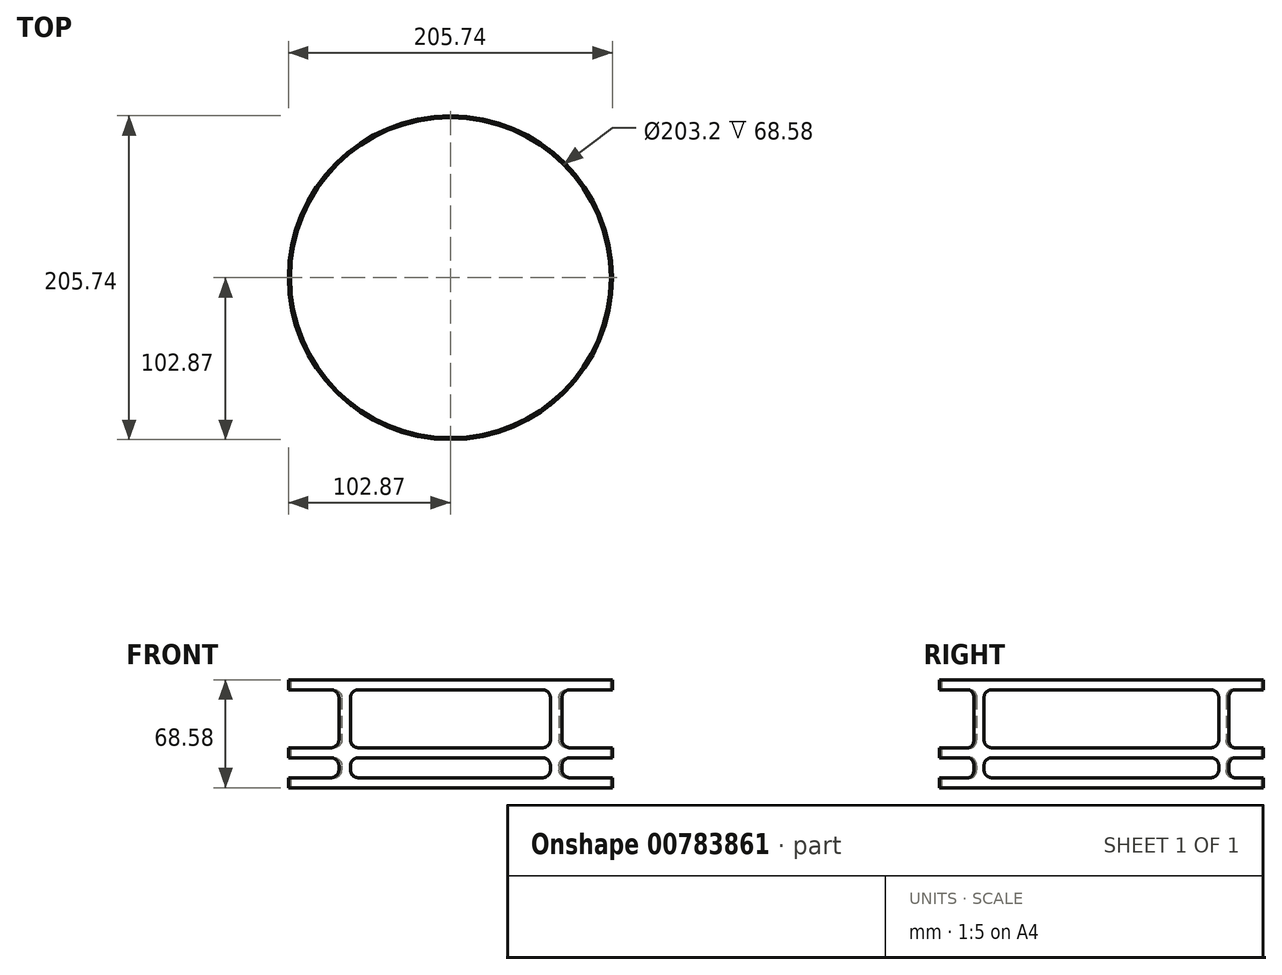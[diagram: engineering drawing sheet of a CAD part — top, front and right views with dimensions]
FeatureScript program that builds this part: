
annotation { "Feature Type Name" : "Feature", "Feature Type Description" : "" }
export const myFeature = defineFeature(function(context is Context, id is Id, definition is map)
    precondition{}
    {
        {
            var Q0;
            Q0=qCreatedBy(makeId("Top.planeOp"),FACE);
            var sketch = newSketch(context, id + "F0", { "sketchPlane" : qUnion([Q0])});
            skCircle(sketch, "E0", {"center": v(0, 0) * mm, "radius": 101.6 * mm});
            skCircle(sketch, "E1", {"center": v(0, 0) * mm, "radius": 102.87 * mm});
            skSolve(sketch);
        }
        {
            var Q0;
            Q0 = qSketchRegion(id + "F0", true);
            extrude(context, id + "F1", {"entities" : qUnion([Q0]), "depth" : 68.58 * mm, "offsetDistance" : 25.4 * mm});
        }
        {
            var Q0;
            Q0=qCreatedBy(makeId("Front.planeOp"),FACE);
            var sketch = newSketch(context, id + "F2", { "sketchPlane" : qUnion([Q0])});
            skLineSegment(sketch, "E2", {"start": v(-102.87, 0) * mm, "end": v(-102.87, 68.58) * mm, "construction": true});
            skLineSegment(sketch, "E3", {"start": v(102.87, 68.58) * mm, "end": v(102.87, 0) * mm, "construction": true});
            skLineSegment(sketch, "E4.0", {"start": v(-102.87, 0) * mm, "end": v(102.87, 0) * mm, "construction": true});
            skLineSegment(sketch, "E5", {"start": v(0, 0) * mm, "end": v(0, 25.4) * mm, "construction": true});
            skLineSegment(sketch, "E6.bottom", {"start": v(63.5, 6.35) * mm, "end": v(-63.5, 6.35) * mm});
            skLineSegment(sketch, "E6.top", {"start": v(63.5, 19.05) * mm, "end": v(-63.5, 19.05) * mm});
            skLineSegment(sketch, "E6.left", {"start": v(63.5, 6.35) * mm, "end": v(63.5, 19.05) * mm});
            skLineSegment(sketch, "E6.right", {"start": v(-63.5, 6.35) * mm, "end": v(-63.5, 19.05) * mm});
            skPoint(sketch, "E6.middle", {"position": v(0, 12.7) * mm});
            skLineSegment(sketch, "E7.0", {"start": v(-102.87, 68.58) * mm, "end": v(102.87, 68.58) * mm, "construction": true});
            skLineSegment(sketch, "E8", {"start": v(-63.5, 25.4) * mm, "end": v(-63.5, 62.23) * mm});
            skLineSegment(sketch, "E9", {"start": v(-63.5, 62.23) * mm, "end": v(63.5, 62.23) * mm});
            skLineSegment(sketch, "E10", {"start": v(63.5, 62.23) * mm, "end": v(63.5, 25.4) * mm});
            skLineSegment(sketch, "E11", {"start": v(63.5, 25.4) * mm, "end": v(-63.5, 25.4) * mm});
            skPoint(sketch, "E12.orphan", {"position": v(-63.5, 27.25) * mm});
            skSolve(sketch);
        }
        {
            var Q0;
            Q0 = qSketchRegion(id + "F2", true);
            extrude(context, id + "F3", {"entities" : qUnion([Q0]), "operationType" : NewBodyOperationType.REMOVE, "endBound" : BoundingType.THROUGH_ALL, "oppositeDirection" : true, "depth" : 25.4 * mm, "offsetDistance" : 25.4 * mm, "hasSecondDirection" : true, "secondDirectionBound" : BoundingType.THROUGH_ALL, "secondDirectionOppositeDirection" : false, "secondDirectionDepth" : 25.4 * mm});
        }
        {
            var Q0;
            Q0=qCreatedBy(makeId("Right.planeOp"),FACE);
            var sketch = newSketch(context, id + "F4", { "sketchPlane" : qUnion([Q0])});
            skLineSegment(sketch, "E13", {"start": v(-102.87, 0) * mm, "end": v(-102.87, 68.58) * mm, "construction": true});
            skLineSegment(sketch, "E14", {"start": v(102.87, 68.58) * mm, "end": v(102.87, 0) * mm, "construction": true});
            skLineSegment(sketch, "E15", {"start": v(0, 0) * mm, "end": v(0, 25.4) * mm, "construction": true});
            skLineSegment(sketch, "E16.bottom", {"start": v(74.58, 6.35) * mm, "end": v(-74.58, 6.35) * mm});
            skLineSegment(sketch, "E16.top", {"start": v(74.58, 19.05) * mm, "end": v(-74.58, 19.05) * mm});
            skLineSegment(sketch, "E16.left", {"start": v(74.58, 6.35) * mm, "end": v(74.58, 19.05) * mm});
            skLineSegment(sketch, "E16.right", {"start": v(-74.58, 6.35) * mm, "end": v(-74.58, 19.05) * mm});
            skPoint(sketch, "E16.middle", {"position": v(0, 12.7) * mm});
            skLineSegment(sketch, "E17.0", {"start": v(-102.87, 68.58) * mm, "end": v(102.87, 68.58) * mm, "construction": true});
            skLineSegment(sketch, "E18.0", {"start": v(-80.93, 25.4) * mm, "end": v(-80.93, 62.23) * mm, "construction": true});
            skLineSegment(sketch, "E19.0", {"start": v(80.93, 62.23) * mm, "end": v(80.93, 25.4) * mm, "construction": true});
            skLineSegment(sketch, "E20.bottom", {"start": v(-74.58, 25.4) * mm, "end": v(74.58, 25.4) * mm});
            skLineSegment(sketch, "E20.top", {"start": v(-74.58, 62.23) * mm, "end": v(74.58, 62.23) * mm});
            skLineSegment(sketch, "E20.left", {"start": v(-74.58, 25.4) * mm, "end": v(-74.58, 62.23) * mm});
            skLineSegment(sketch, "E20.right", {"start": v(74.58, 25.4) * mm, "end": v(74.58, 62.23) * mm});
            skSolve(sketch);
        }
        {
            var Q0;
            Q0 = qSketchRegion(id + "F4", true);
            extrude(context, id + "F5", {"entities" : qUnion([Q0]), "operationType" : NewBodyOperationType.REMOVE, "endBound" : BoundingType.THROUGH_ALL, "oppositeDirection" : true, "depth" : 25.4 * mm, "offsetDistance" : 25.4 * mm, "hasSecondDirection" : true, "secondDirectionBound" : BoundingType.THROUGH_ALL, "secondDirectionOppositeDirection" : false, "secondDirectionDepth" : 25.4 * mm});
        }
        {
            var Q0;
            Q0=makeQuery(id+"F3.boolean.opBoolean","COPY",EDGE,{"disambiguationData":[OD(0.0)],"derivedFrom":makeQuery(id+"F3.opExtrude","SWEPT_EDGE",EDGE,{"disambiguationData":[OSD([sQuery(id+"F2.wireOp",EDGE,"E6.top"),sQuery(id+"F2.wireOp",EDGE,"E6.right")])]})});
            var Q1;
            Q1=makeQuery(id+"F3.boolean.opBoolean","COPY",EDGE,{"disambiguationData":[OD(0.0)],"derivedFrom":makeQuery(id+"F3.opExtrude","SWEPT_EDGE",EDGE,{"disambiguationData":[OSD([sQuery(id+"F2.wireOp",EDGE,"E6.bottom"),sQuery(id+"F2.wireOp",EDGE,"E6.right")])]})});
            var Q2;
            Q2=makeQuery(id+"F3.boolean.opBoolean","COPY",EDGE,{"disambiguationData":[OD(0.0)],"derivedFrom":makeQuery(id+"F3.opExtrude","SWEPT_EDGE",EDGE,{"disambiguationData":[OSD([sQuery(id+"F2.wireOp",EDGE,"E6.top"),sQuery(id+"F2.wireOp",EDGE,"E6.left")])]})});
            var Q3;
            Q3=makeQuery(id+"F3.boolean.opBoolean","COPY",EDGE,{"disambiguationData":[OD(0.0)],"derivedFrom":makeQuery(id+"F3.opExtrude","SWEPT_EDGE",EDGE,{"disambiguationData":[OSD([sQuery(id+"F2.wireOp",EDGE,"E6.bottom"),sQuery(id+"F2.wireOp",EDGE,"E6.left")])]})});
            var Q4;
            Q4=makeQuery(id+"F5.boolean.opBoolean","COPY",EDGE,{"disambiguationData":[OD(1.0)],"derivedFrom":makeQuery(id+"F5.opExtrude","SWEPT_EDGE",EDGE,{"disambiguationData":[OSD([sQuery(id+"F4.wireOp",EDGE,"E16.top"),sQuery(id+"F4.wireOp",EDGE,"E16.right")])]})});
            var Q5;
            Q5=makeQuery(id+"F5.boolean.opBoolean","COPY",EDGE,{"disambiguationData":[OD(1.0)],"derivedFrom":makeQuery(id+"F5.opExtrude","SWEPT_EDGE",EDGE,{"disambiguationData":[OSD([sQuery(id+"F4.wireOp",EDGE,"E16.bottom"),sQuery(id+"F4.wireOp",EDGE,"E16.right")])]})});
            var Q6;
            Q6=makeQuery(id+"F5.boolean.opBoolean","COPY",EDGE,{"disambiguationData":[OD(1.0)],"derivedFrom":makeQuery(id+"F5.opExtrude","SWEPT_EDGE",EDGE,{"disambiguationData":[OSD([sQuery(id+"F4.wireOp",EDGE,"E16.top"),sQuery(id+"F4.wireOp",EDGE,"E16.left")])]})});
            var Q7;
            Q7=makeQuery(id+"F5.boolean.opBoolean","COPY",EDGE,{"disambiguationData":[OD(1.0)],"derivedFrom":makeQuery(id+"F5.opExtrude","SWEPT_EDGE",EDGE,{"disambiguationData":[OSD([sQuery(id+"F4.wireOp",EDGE,"E16.bottom"),sQuery(id+"F4.wireOp",EDGE,"E16.left")])]})});
            var Q8;
            Q8=makeQuery(id+"F3.boolean.opBoolean","COPY",EDGE,{"disambiguationData":[OD(1.0)],"derivedFrom":makeQuery(id+"F3.opExtrude","SWEPT_EDGE",EDGE,{"disambiguationData":[OSD([sQuery(id+"F2.wireOp",EDGE,"E6.bottom"),sQuery(id+"F2.wireOp",EDGE,"E6.left")])]})});
            var Q9;
            Q9=makeQuery(id+"F3.boolean.opBoolean","COPY",EDGE,{"disambiguationData":[OD(1.0)],"derivedFrom":makeQuery(id+"F3.opExtrude","SWEPT_EDGE",EDGE,{"disambiguationData":[OSD([sQuery(id+"F2.wireOp",EDGE,"E6.top"),sQuery(id+"F2.wireOp",EDGE,"E6.left")])]})});
            var Q10;
            Q10=makeQuery(id+"F3.boolean.opBoolean","COPY",EDGE,{"disambiguationData":[OD(1.0)],"derivedFrom":makeQuery(id+"F3.opExtrude","SWEPT_EDGE",EDGE,{"disambiguationData":[OSD([sQuery(id+"F2.wireOp",EDGE,"E6.bottom"),sQuery(id+"F2.wireOp",EDGE,"E6.right")])]})});
            var Q11;
            Q11=makeQuery(id+"F3.boolean.opBoolean","COPY",EDGE,{"disambiguationData":[OD(1.0)],"derivedFrom":makeQuery(id+"F3.opExtrude","SWEPT_EDGE",EDGE,{"disambiguationData":[OSD([sQuery(id+"F2.wireOp",EDGE,"E6.top"),sQuery(id+"F2.wireOp",EDGE,"E6.right")])]})});
            var Q12;
            Q12=makeQuery(id+"F5.boolean.opBoolean","COPY",EDGE,{"disambiguationData":[OD(0.0)],"derivedFrom":makeQuery(id+"F5.opExtrude","SWEPT_EDGE",EDGE,{"disambiguationData":[OSD([sQuery(id+"F4.wireOp",EDGE,"E16.bottom"),sQuery(id+"F4.wireOp",EDGE,"E16.left")])]})});
            var Q13;
            Q13=makeQuery(id+"F5.boolean.opBoolean","COPY",EDGE,{"disambiguationData":[OD(0.0)],"derivedFrom":makeQuery(id+"F5.opExtrude","SWEPT_EDGE",EDGE,{"disambiguationData":[OSD([sQuery(id+"F4.wireOp",EDGE,"E16.top"),sQuery(id+"F4.wireOp",EDGE,"E16.left")])]})});
            var Q14;
            Q14=makeQuery(id+"F5.boolean.opBoolean","COPY",EDGE,{"disambiguationData":[OD(0.0)],"derivedFrom":makeQuery(id+"F5.opExtrude","SWEPT_EDGE",EDGE,{"disambiguationData":[OSD([sQuery(id+"F4.wireOp",EDGE,"E16.bottom"),sQuery(id+"F4.wireOp",EDGE,"E16.right")])]})});
            var Q15;
            Q15=makeQuery(id+"F5.boolean.opBoolean","COPY",EDGE,{"disambiguationData":[OD(0.0)],"derivedFrom":makeQuery(id+"F5.opExtrude","SWEPT_EDGE",EDGE,{"disambiguationData":[OSD([sQuery(id+"F4.wireOp",EDGE,"E16.top"),sQuery(id+"F4.wireOp",EDGE,"E16.right")])]})});
            var Q16;
            Q16=makeQuery(id+"F3.boolean.opBoolean","COPY",EDGE,{"disambiguationData":[OD(0.0)],"derivedFrom":makeQuery(id+"F3.opExtrude","SWEPT_EDGE",EDGE,{"disambiguationData":[OSD([sQuery(id+"F2.wireOp",EDGE,"E8"),sQuery(id+"F2.wireOp",EDGE,"E11")])]})});
            var Q17;
            Q17=makeQuery(id+"F3.boolean.opBoolean","COPY",EDGE,{"disambiguationData":[OD(0.0)],"derivedFrom":makeQuery(id+"F3.opExtrude","SWEPT_EDGE",EDGE,{"disambiguationData":[OSD([sQuery(id+"F2.wireOp",EDGE,"E8"),sQuery(id+"F2.wireOp",EDGE,"E9")])]})});
            var Q18;
            Q18=makeQuery(id+"F3.boolean.opBoolean","COPY",EDGE,{"disambiguationData":[OD(0.0)],"derivedFrom":makeQuery(id+"F3.opExtrude","SWEPT_EDGE",EDGE,{"disambiguationData":[OSD([sQuery(id+"F2.wireOp",EDGE,"E10"),sQuery(id+"F2.wireOp",EDGE,"E11")])]})});
            var Q19;
            Q19=makeQuery(id+"F3.boolean.opBoolean","COPY",EDGE,{"disambiguationData":[OD(0.0)],"derivedFrom":makeQuery(id+"F3.opExtrude","SWEPT_EDGE",EDGE,{"disambiguationData":[OSD([sQuery(id+"F2.wireOp",EDGE,"E9"),sQuery(id+"F2.wireOp",EDGE,"E10")])]})});
            var Q20;
            Q20=makeQuery(id+"F5.boolean.opBoolean","COPY",EDGE,{"disambiguationData":[OD(0.0)],"derivedFrom":makeQuery(id+"F5.opExtrude","SWEPT_EDGE",EDGE,{"disambiguationData":[OSD([sQuery(id+"F4.wireOp",EDGE,"E20.top"),sQuery(id+"F4.wireOp",EDGE,"E20.left")])]})});
            var Q21;
            Q21=makeQuery(id+"F5.boolean.opBoolean","COPY",EDGE,{"disambiguationData":[OD(0.0)],"derivedFrom":makeQuery(id+"F5.opExtrude","SWEPT_EDGE",EDGE,{"disambiguationData":[OSD([sQuery(id+"F4.wireOp",EDGE,"E20.bottom"),sQuery(id+"F4.wireOp",EDGE,"E20.left")])]})});
            var Q22;
            Q22=makeQuery(id+"F5.boolean.opBoolean","COPY",EDGE,{"disambiguationData":[OD(0.0)],"derivedFrom":makeQuery(id+"F5.opExtrude","SWEPT_EDGE",EDGE,{"disambiguationData":[OSD([sQuery(id+"F4.wireOp",EDGE,"E20.top"),sQuery(id+"F4.wireOp",EDGE,"E20.right")])]})});
            var Q23;
            Q23=makeQuery(id+"F5.boolean.opBoolean","COPY",EDGE,{"disambiguationData":[OD(0.0)],"derivedFrom":makeQuery(id+"F5.opExtrude","SWEPT_EDGE",EDGE,{"disambiguationData":[OSD([sQuery(id+"F4.wireOp",EDGE,"E20.bottom"),sQuery(id+"F4.wireOp",EDGE,"E20.right")])]})});
            var Q24;
            Q24=makeQuery(id+"F3.boolean.opBoolean","COPY",EDGE,{"disambiguationData":[OD(1.0)],"derivedFrom":makeQuery(id+"F3.opExtrude","SWEPT_EDGE",EDGE,{"disambiguationData":[OSD([sQuery(id+"F2.wireOp",EDGE,"E8"),sQuery(id+"F2.wireOp",EDGE,"E9")])]})});
            var Q25;
            Q25=makeQuery(id+"F3.boolean.opBoolean","COPY",EDGE,{"disambiguationData":[OD(1.0)],"derivedFrom":makeQuery(id+"F3.opExtrude","SWEPT_EDGE",EDGE,{"disambiguationData":[OSD([sQuery(id+"F2.wireOp",EDGE,"E8"),sQuery(id+"F2.wireOp",EDGE,"E11")])]})});
            var Q26;
            Q26=makeQuery(id+"F3.boolean.opBoolean","COPY",EDGE,{"disambiguationData":[OD(1.0)],"derivedFrom":makeQuery(id+"F3.opExtrude","SWEPT_EDGE",EDGE,{"disambiguationData":[OSD([sQuery(id+"F2.wireOp",EDGE,"E9"),sQuery(id+"F2.wireOp",EDGE,"E10")])]})});
            var Q27;
            Q27=makeQuery(id+"F3.boolean.opBoolean","COPY",EDGE,{"disambiguationData":[OD(1.0)],"derivedFrom":makeQuery(id+"F3.opExtrude","SWEPT_EDGE",EDGE,{"disambiguationData":[OSD([sQuery(id+"F2.wireOp",EDGE,"E10"),sQuery(id+"F2.wireOp",EDGE,"E11")])]})});
            var Q28;
            Q28=makeQuery(id+"F5.boolean.opBoolean","COPY",EDGE,{"disambiguationData":[OD(1.0)],"derivedFrom":makeQuery(id+"F5.opExtrude","SWEPT_EDGE",EDGE,{"disambiguationData":[OSD([sQuery(id+"F4.wireOp",EDGE,"E20.bottom"),sQuery(id+"F4.wireOp",EDGE,"E20.right")])]})});
            var Q29;
            Q29=makeQuery(id+"F5.boolean.opBoolean","COPY",EDGE,{"disambiguationData":[OD(1.0)],"derivedFrom":makeQuery(id+"F5.opExtrude","SWEPT_EDGE",EDGE,{"disambiguationData":[OSD([sQuery(id+"F4.wireOp",EDGE,"E20.top"),sQuery(id+"F4.wireOp",EDGE,"E20.right")])]})});
            var Q30;
            Q30=makeQuery(id+"F5.boolean.opBoolean","COPY",EDGE,{"disambiguationData":[OD(1.0)],"derivedFrom":makeQuery(id+"F5.opExtrude","SWEPT_EDGE",EDGE,{"disambiguationData":[OSD([sQuery(id+"F4.wireOp",EDGE,"E20.top"),sQuery(id+"F4.wireOp",EDGE,"E20.left")])]})});
            var Q31;
            Q31=makeQuery(id+"F5.boolean.opBoolean","COPY",EDGE,{"disambiguationData":[OD(1.0)],"derivedFrom":makeQuery(id+"F5.opExtrude","SWEPT_EDGE",EDGE,{"disambiguationData":[OSD([sQuery(id+"F4.wireOp",EDGE,"E20.bottom"),sQuery(id+"F4.wireOp",EDGE,"E20.left")])]})});
            fillet(context, id + "F6", {"entities" : qUnion([Q0, Q1, Q2, Q3, Q4, Q5, Q6, Q7, Q8, Q9, Q10, Q11, Q12, Q13, Q14, Q15, Q16, Q17, Q18, Q19, Q20, Q21, Q22, Q23, Q24, Q25, Q26, Q27, Q28, Q29, Q30, Q31]), "radius" : 5.08 * mm, "tangentPropagation" : true, "allowEdgeOverflow" : false});
        }
    });
